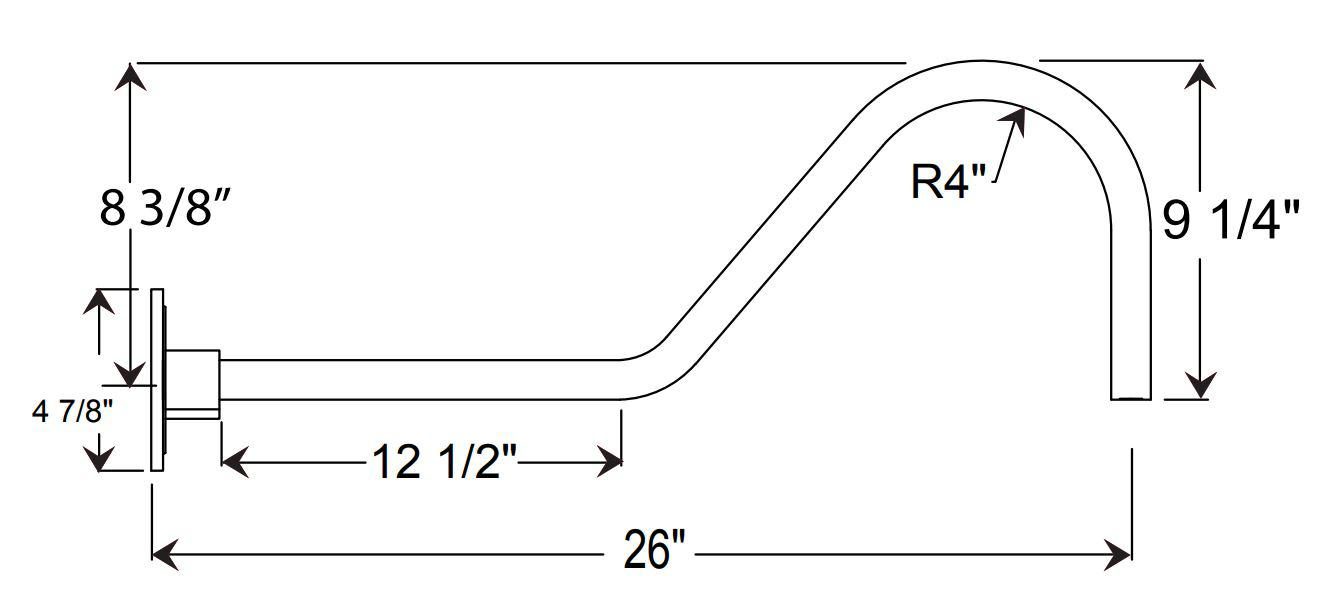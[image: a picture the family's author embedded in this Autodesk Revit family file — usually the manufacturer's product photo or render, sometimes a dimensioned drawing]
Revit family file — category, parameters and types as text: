
# Revit family: OSOC MB 20
name_source: partatom
category: Lighting Fixtures
units: mm (PartAtom-declared; Revit-internal decimal feet)

## family parameters
Always vertical = Yes
Cut with Voids When Loaded = No
Light Source = Yes
OmniClass Number = 23.80.70.00
OmniClass Title = Lighting
Part Type = Normal
Room Calculation Point = No
Round Connector Dimension = Use Diameter
Shared = No
Work Plane-Based = No

## types (1)
- OSOC20
    Apparent Load = 200 VA
    Body Colour = Spun aluminium
    Body Material = body
    CRI = >90
    Canopy Body = body
    Color Filter = 16777215
    Construction Material = Heavy Duty spun aluminum.
    Default Elevation = 0' - 0"
    Description = 120-277 Voltage
    Dimming = 1%
    Dimming Lamp Color Temperature Shift = <None>
    Efficiency = 65-125 lumens per watt
    Fixture Diameter = 1' - 8"
    Fixture Height = 1' - 7 3/4"
    GLASS = Glass
    HUB = body
    Lamp = MB
    Life = L70 50,000 hours
    Load Classification = Lighting
    Manufacturer = ANP Lighting
    Model = OSOC20
    OSOC20 = Yes
    Photometric Web File = generic
    Power Factor = 1
    Ring = body
    Tilt Angle = 90.00°
    URL = https://www.anplighting.com
    Voltage = 120 V
    Warranty = 5 year limited warranty
    Wattage Comments = 200 W
    Weight = 18.0 lbs
    a = 1' - 7"
    b = 0' - 3"

## geometry (parser evidence)
native form markers: Sweep x22
no freeform markers — native parametric forms only
